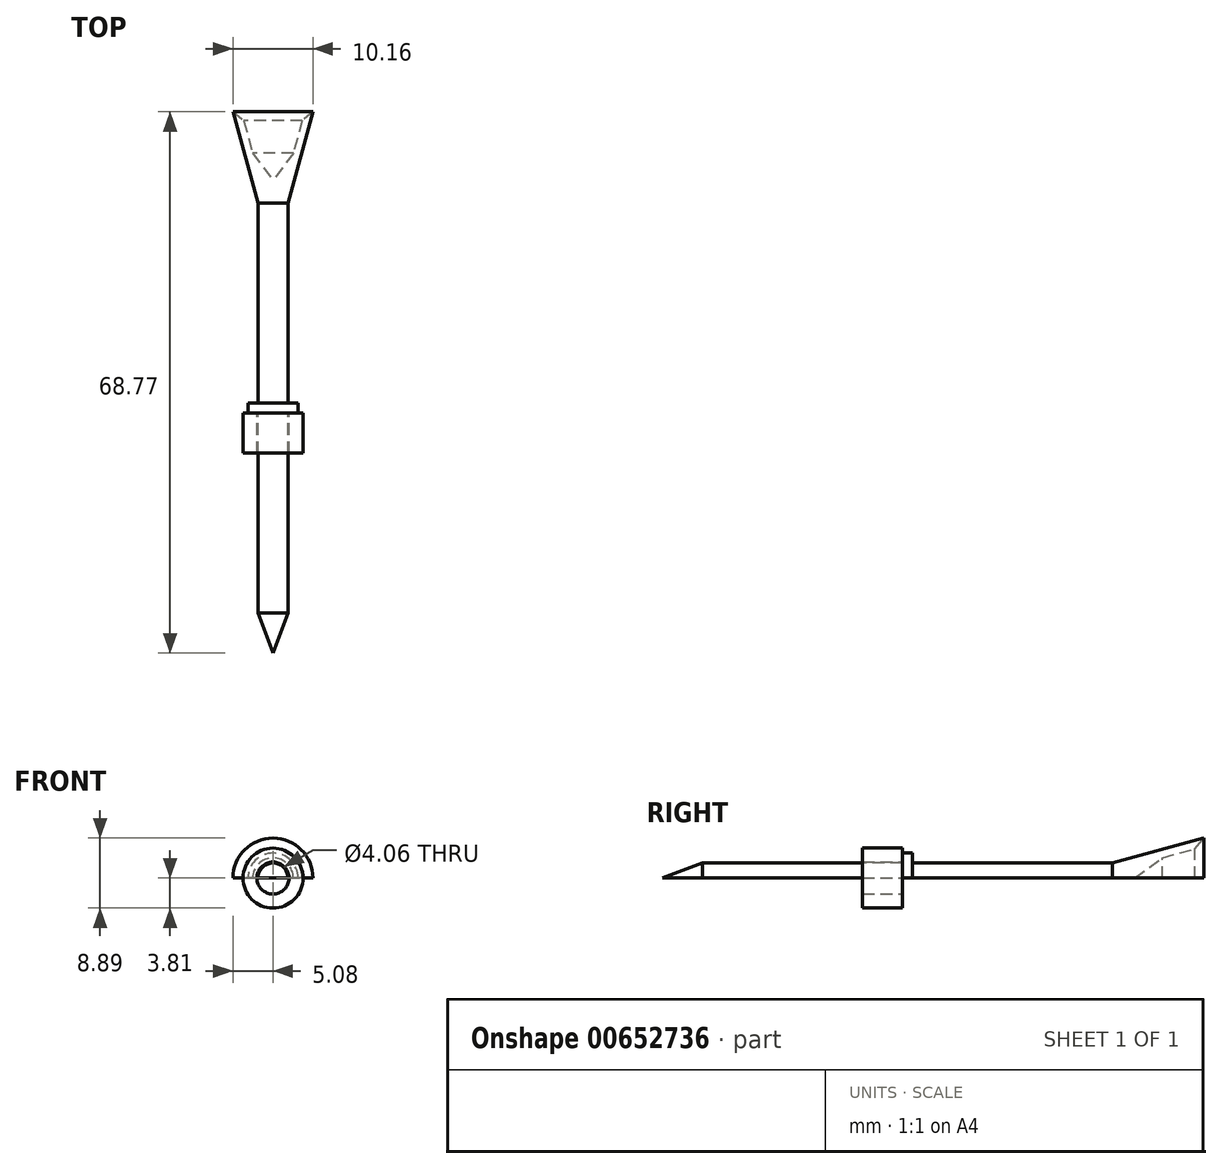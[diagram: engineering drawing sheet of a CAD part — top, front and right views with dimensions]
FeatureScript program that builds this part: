
annotation { "Feature Type Name" : "Feature", "Feature Type Description" : "" }
export const myFeature = defineFeature(function(context is Context, id is Id, definition is map)
    precondition{}
    {
        {
            var Q0;
            Q0=qCreatedBy(makeId("Top.planeOp"),FACE);
            var sketch = newSketch(context, id + "F0", { "sketchPlane" : qUnion([Q0])});
            skLineSegment(sketch, "E0", {"start": v(0, 0) * mm, "end": v(0, 60.03) * mm});
            skLineSegment(sketch, "E1", {"start": v(-1.9, 5.08) * mm, "end": v(0, 0) * mm});
            skLineSegment(sketch, "E2", {"start": v(-1.9, 5.08) * mm, "end": v(-1.9, 30.48) * mm});
            skLineSegment(sketch, "E3", {"start": v(-1.9, 57.15) * mm, "end": v(-5.08, 68.77) * mm});
            skLineSegment(sketch, "E4", {"start": v(-1.9, 31.75) * mm, "end": v(-3.18, 31.75) * mm});
            skLineSegment(sketch, "E5", {"start": v(-3.18, 31.75) * mm, "end": v(-3.18, 30.48) * mm});
            skLineSegment(sketch, "E6", {"start": v(-3.18, 30.48) * mm, "end": v(-1.9, 30.48) * mm});
            skLineSegment(sketch, "E7.trimOffspring", {"start": v(-1.9, 31.75) * mm, "end": v(-1.9, 57.15) * mm});
            skLineSegment(sketch, "E8", {"start": v(-5.08, 68.77) * mm, "end": v(-3.7, 67.62) * mm});
            skLineSegment(sketch, "E9", {"start": v(-3.7, 67.62) * mm, "end": v(-2.58, 63.5) * mm});
            skLineSegment(sketch, "E10", {"start": v(-2.58, 63.5) * mm, "end": v(0, 60.03) * mm});
            skPoint(sketch, "E11.orphan", {"position": v(0, 63.5) * mm});
            skSolve(sketch);
        }
        {
            var Q0;
            Q0=makeQuery(id+"F0.imprint","IMPRINT",FACE,{"disambiguationData":[TD([[makeQuery(id+"F0.imprint","IMPRINT",EDGE,{"derivedFrom":sQuery(id+"F0.wireOp",EDGE,"E0")}),1.0]])]});
            var Q1;
            Q1=sQuery(id+"F0.wireOp",EDGE,"E0");
            revolve(context, id + "F1", {"entities" : qUnion([Q0]), "axis" : qUnion([Q1]), "revolveType" : RevolveType.ONE_DIRECTION, "angle" : 180 * degree});
        }
        {
            var Q0;
            Q0=makeQuery(id+"F1.opRevolve","SWEPT_FACE",FACE,{"disambiguationData":[OSD([sQuery(id+"F0.wireOp",EDGE,"E6")])]});
            var sketch = newSketch(context, id + "F2", { "sketchPlane" : qUnion([Q0])});
            skCircle(sketch, "E12", {"center": v(0, 0) * mm, "radius": 3.81 * mm});
            skCircle(sketch, "E13", {"center": v(0, 0) * mm, "radius": 2.03 * mm});
            skSolve(sketch);
        }
        {
            var Q0;
            Q0=makeQuery(id+"F2.imprint","IMPRINT",FACE,{"disambiguationData":[TD([[makeQuery(id+"F2.imprint","IMPRINT",EDGE,{"derivedFrom":sQuery(id+"F2.wireOp",EDGE,"E12")}),1.0]])]});
            var Q1;
            {var subQ1=sQuery(id+"F0.wireOp",EDGE,"E6");var subQ6=makeQuery(id+"F1.opRevolve","SWEPT_EDGE",EDGE,{"disambiguationData":[OSD([sQuery(id+"F0.wireOp",EDGE,"E5"),subQ1])]});Q1=makeQuery(id+"F2.imprint","IMPRINT",FACE,{"disambiguationData":[TD([[makeQuery(id+"F2.imprint","IMPRINT",EDGE,{"derivedFrom":subQ6}),1.0]])]});}
            extrude(context, id + "F3", {"entities" : qUnion([Q0, Q1]), "depth" : 5.08 * mm, "offsetDistance" : 25.4 * mm});
        }
    });
